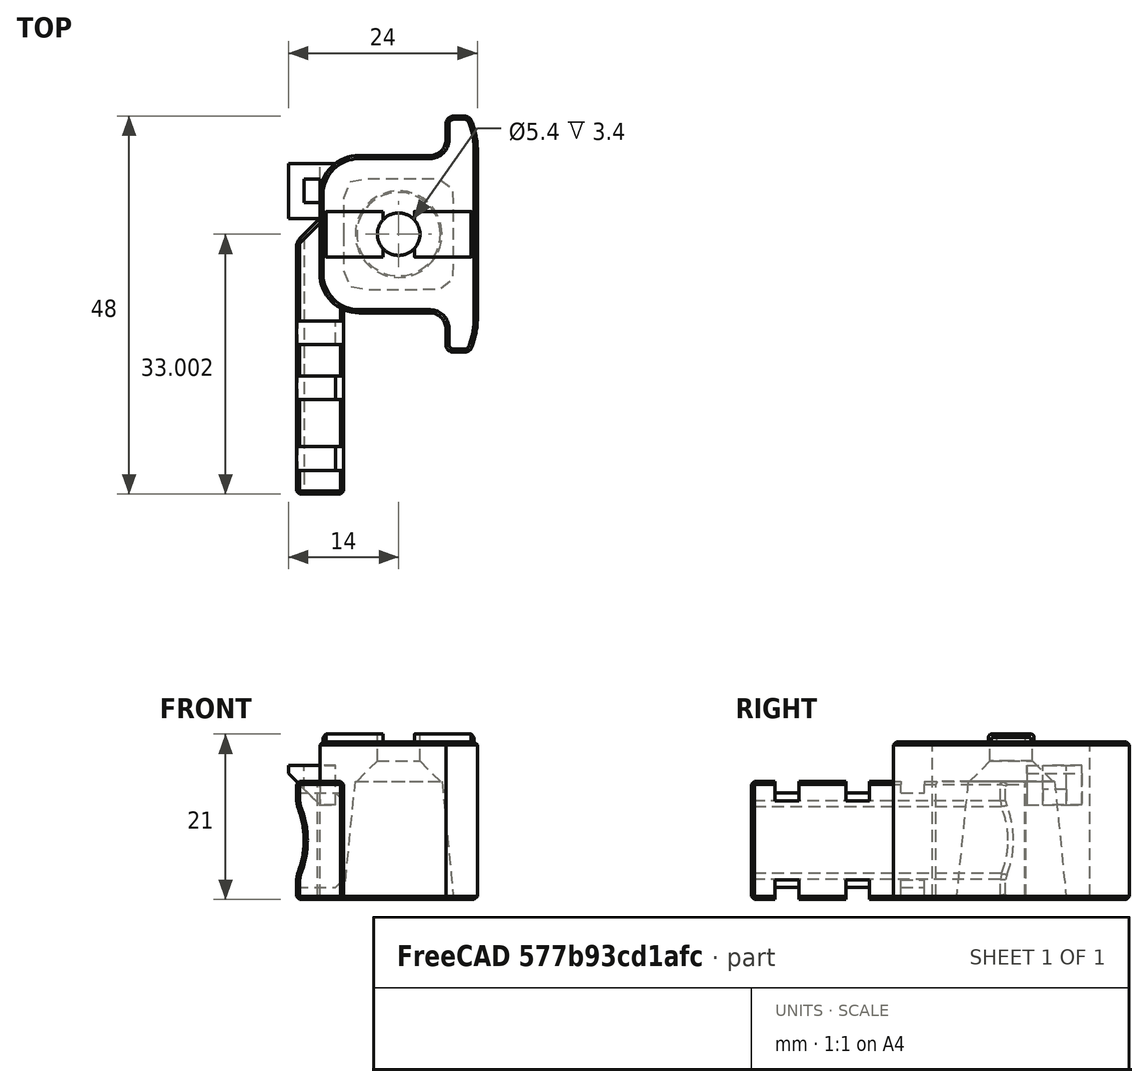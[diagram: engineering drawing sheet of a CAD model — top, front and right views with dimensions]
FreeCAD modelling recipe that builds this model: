
FCSTD DOCUMENT  (FreeCAD 0.18R16146 (Git))
Label: toolhead-cable-end
License: Other
LicenseURL: GPL3
objects: Part::Box×6, Part::Chamfer×5, Part::Cut×3, Part::MultiFuse×3, Part::Feature×2, Part::Cylinder×1
note: 20 computed .brp shape members not serialized (recipe doc carries the construction recipe); baked Part::Feature solids carry a one-line shape summary decoded from their .brp

FEATURE [Part::Feature] Part__Feature691  label="Z_Chain_Guide"
  Placement = pos=(10.0004,7.50215,19.996) rot=(0.57735,0.57735,-0.57735;2.0944rad)
  shape: bbox 20 x 30 x 21 mm, 87 faces (baked)
FEATURE [Part::Box] Box  label="Cube"
  AttacherType = Attacher::AttachEngine3D
  Height = 15
  Length = 6
  Placement = pos=(-3,-32,0) rot=(0,0,1;0rad)
  Width = 35
FEATURE [Part::Cylinder] Cylinder
  Angle = 360
  AttacherType = Attacher::AttachEngine3D
  Height = 49
  Placement = pos=(-13,4,7.5) rot=(1,0,0;1.5708rad)
  Radius = 11
FEATURE [Part::Chamfer] Chamfer
  Base = -> Box
  Edges = 1 edges r=3: [Edge3]
FEATURE [Part::Cut] Cut
  Base = -> Chamfer
  Tool = -> Cylinder
FEATURE [Part::Chamfer] Chamfer001
  Base = -> Cut
  Edges = 4 edges r=0.4: [Edge2,Edge4,Edge20,Edge24]
FEATURE [Part::Chamfer] Chamfer002
  Base = -> Chamfer001
  Edges = 24 edges r=0.4: [Edge1,Edge4,Edge5,Edge6,Edge7,Edge8,Edge9,Edge10,Edge11,Edge12,Edge13,Edge14,Edge16,Edge17,Edge19,Edge20,Edge21,Edge22,Edge23,Edge24,Edge25,Edge26,Edge29,Edge34]
FEATURE [Part::Box] Box001  label="Cube001"
  AttacherType = Attacher::AttachEngine3D
  Height = 20
  Length = 5
  Placement = pos=(-14,-20,1.5) rot=(0,1,0;1.5708rad)
  Width = 3
FEATURE [Part::Box] Box002  label="Cube002"
  AttacherType = Attacher::AttachEngine3D
  Height = 20
  Length = 5
  Placement = pos=(-14,-29,1.5) rot=(0,1,0;1.5708rad)
  Width = 3
FEATURE [Part::Box] Box003  label="Cube003"
  AttacherType = Attacher::AttachEngine3D
  Height = 20
  Length = 5
  Placement = pos=(-14,-13,1.5) rot=(0,1,0;1.5708rad)
  Width = 3
FEATURE [Part::MultiFuse] Fusion
  Shapes = -> [Box003,Box002,Box001]
FEATURE [Part::Feature] Fusion001
  Placement = pos=(0,0,17) rot=(0,0,1;0rad)
  shape: bbox 20 x 19 x 5 mm, 18 faces, 3 solids (baked)
FEATURE [Part::MultiFuse] Fusion002
  Shapes = -> [Fusion001,Fusion]
FEATURE [Part::Cut] Cut001
  Base = -> Chamfer002
  Tool = -> Fusion002
FEATURE [Part::Chamfer] Chamfer003
  Base = -> Cut001
  Edges = 5 edges r=1: [Edge33,Edge45,Edge94,Edge98,Edge102]
  Placement = pos=(0,-1,0) rot=(0,0,1;0rad)
FEATURE [Part::Box] Box004  label="Cube004"
  AttacherType = Attacher::AttachEngine3D
  Height = 15
  Length = 2
  Placement = pos=(-2,4,10) rot=(0,0,1;0rad)
  Width = 3
FEATURE [Part::Box] Box005  label="Cube005"
  AttacherType = Attacher::AttachEngine3D
  Height = 5
  Length = 7
  Placement = pos=(-4,2,15) rot=(0,0,1;0rad)
  Width = 7
FEATURE [Part::Chamfer] Chamfer004
  Base = -> Box005
  Edges = 1 edges r=4: [Edge4]
  Placement = pos=(0,0,-3) rot=(0,0,1;0rad)
FEATURE [Part::Cut] Cut002
  Base = -> Chamfer004
  Tool = -> Box004
FEATURE [Part::MultiFuse] Fusion003
  Shapes = -> [Chamfer003,Part__Feature691,Cut002]
